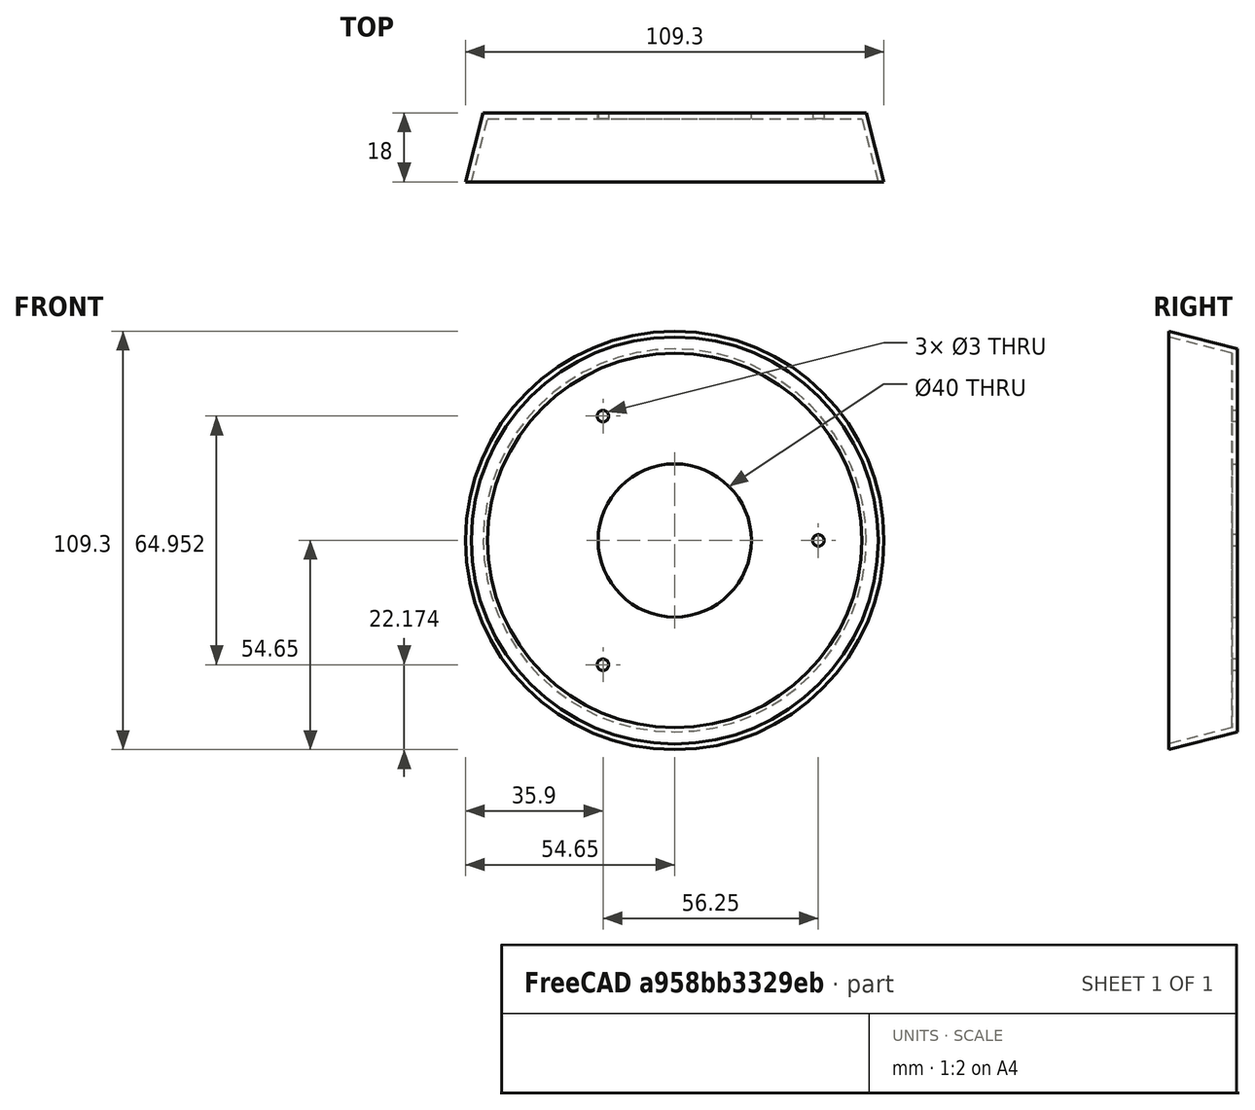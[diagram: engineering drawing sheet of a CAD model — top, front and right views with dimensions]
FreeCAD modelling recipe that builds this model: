
FCSTD DOCUMENT  (FreeCAD 0.18.4R)
Label: radiation_shield_dish
License: All rights reserved
LicenseURL: http://en.wikipedia.org/wiki/All_rights_reserved
objects: TechDraw::DrawViewDimension×5, Sketcher::SketchObject×4, TechDraw::DrawViewPart×3, PartDesign::Revolution×1, PartDesign::Hole×1, PartDesign::Pocket×1, PartDesign::Body×1, App::Part×1, TechDraw::DrawSVGTemplate×1, TechDraw::DrawViewAnnotation×1, TechDraw::DrawPage×1
note: 11 computed .brp shape members not serialized (recipe doc carries the construction recipe); baked Part::Feature solids carry a one-line shape summary decoded from their .brp

FEATURE [Sketcher::SketchObject] Sketch
  sketch-geometry (6):
    g0: LineSegment StartX=-54.6463 StartY=0 StartZ=0 EndX=-53.1463 EndY=0 EndZ=0
    g1: LineSegment StartX=-53.1463 StartY=0 StartZ=0 EndX=-48.8872 EndY=16.5 EndZ=0
    g2: LineSegment StartX=-48.8872 StartY=16.5 StartZ=0 EndX=0 EndY=16.5 EndZ=0
    g3: LineSegment StartX=0 StartY=16.5 StartZ=0 EndX=0 EndY=18 EndZ=0
    g4: LineSegment StartX=0 StartY=18 StartZ=0 EndX=-50 EndY=18 EndZ=0
    g5: LineSegment StartX=-50 StartY=18 StartZ=0 EndX=-54.6463 EndY=0 EndZ=0
  constraints (18):
    c: Coincident(g0,g1)
    c: Coincident(g2,g3)
    c: Coincident(g3,g4)
    c: Coincident(g4,g5)
    c: PointOnObject(g2,g-2)
    c: PointOnObject(g3,g-2)
    c: PointOnObject(g0,g-1)
    c: Coincident(g5,g0)
    c: PointOnObject(g0,g-1)
    c: Equal(g0,g3)
    c: DistanceX(g0,g0) = 1.5
    c: Parallel(g4,g-1)
    c: Parallel(g2,g-1)
    c: Coincident(g1,g2)
    c: DistanceX(g4,g4) = 50
    c: Parallel(g5,g1)
    c: DistanceY(g-1,g4) = 18
    c: Distance(g0,g4) = 18.59
FEATURE [PartDesign::Revolution] Revolution
  Angle = 360
  Axis = (0,1,0)
  Base = (0,0,0)
  Profile = -> Sketch
  ReferenceAxis = -> Sketch [V_Axis]
FEATURE [Sketcher::SketchObject] Sketch001
  MapMode = 5
  Placement = pos=(0,18,0) rot=(0,0.707107,0.707107;3.14159rad)
  Support = -> [Revolution]
  sketch-geometry (8):
    g0: LineSegment [constr] StartX=18.75 StartY=32.476 StartZ=0 EndX=-37.5 EndY=0 EndZ=0
    g1: LineSegment [constr] StartX=-37.5 StartY=0 StartZ=0 EndX=18.75 EndY=-32.476 EndZ=0
    g2: LineSegment [constr] StartX=18.75 StartY=-32.476 StartZ=0 EndX=18.75 EndY=32.476 EndZ=0
    g3: Circle [constr] CenterX=0 CenterY=0 CenterZ=0 NormalX=0 NormalY=0 NormalZ=1 AngleXU=0 Radius=37.5
    g4: Circle CenterX=-37.5 CenterY=0 CenterZ=0 NormalX=0 NormalY=0 NormalZ=1 AngleXU=0 Radius=3
    g5: Circle CenterX=18.75 CenterY=32.476 CenterZ=0 NormalX=0 NormalY=0 NormalZ=1 AngleXU=0 Radius=3
    g6: Circle CenterX=18.75 CenterY=-32.476 CenterZ=0 NormalX=0 NormalY=0 NormalZ=1 AngleXU=0 Radius=3
    g7: Circle CenterX=0 CenterY=0 CenterZ=0 NormalX=0 NormalY=0 NormalZ=1 AngleXU=0 Radius=20
  constraints (19):
    c: Coincident(g0,g1)
    c: Coincident(g1,g2)
    c: Coincident(g2,g0)
    c: Equal(g0,g1)
    c: Equal(g0,g2)
    c: PointOnObject(g0,g3)
    c: PointOnObject(g1,g3)
    c: PointOnObject(g2,g3)
    c: PointOnObject(g0,g-1)
    c: Coincident(g3,g-1)
    c: Radius(g3) = 37.5
    c: Radius(g5) = 3
    c: Coincident(g5,g0)
    c: Radius(g6) = 3
    c: Coincident(g6,g1)
    c: Radius(g4) = 3
    c: Coincident(g4,g0)
    c: Radius(g7) = 20  'Innenloch'
    c: Coincident(g7,g-1)
FEATURE [PartDesign::Hole] Hole
  BaseFeature = -> Revolution
  Depth = 25
  DepthType = 0
  Diameter = 3
  DrillPoint = 1
  DrillPointAngle = 118
  HoleCutCountersinkAngle = 90
  HoleCutDepth = 0
  HoleCutDiameter = 0
  HoleCutType = 0
  ModelActualThread = false
  Profile = -> Sketch001
  Tapered = false
  TaperedAngle = 90
  ThreadAngle = 0
  ThreadClass = 0
  ThreadCutOffInner = 0
  ThreadCutOffOuter = 0
  ThreadDirection = 0
  ThreadFit = 0
  ThreadPitch = 0
  ThreadSize = 0
  ThreadType = 0
  Threaded = false
FEATURE [Sketcher::SketchObject] Sketch002
  MapMode = 5
  Placement = pos=(0,18,0) rot=(0,0.707107,0.707107;3.14159rad)
  Support = -> [Hole]
  sketch-geometry (1):
    g0: Circle CenterX=0 CenterY=0 CenterZ=0 NormalX=0 NormalY=0 NormalZ=1 AngleXU=0 Radius=20
  constraints (2):
    c: Radius(g0) = 20  'Innenloch'
    c: Coincident(g0,g-1)
FEATURE [Sketcher::SketchObject] CopySketch002
  Placement = pos=(0,18,0) rot=(0,0.707107,0.707107;3.14159rad)
  sketch-geometry (1):
    g0: Circle CenterX=0 CenterY=0 CenterZ=0 NormalX=0 NormalY=0 NormalZ=1 AngleXU=0 Radius=20
  constraints (2):
    c: Radius(g0) = 20  'Innenloch'
    c: Coincident(g0,g-1)
FEATURE [PartDesign::Pocket] Pocket
  BaseFeature = -> Hole
  Length = 5
  Length2 = 100
  Profile = -> CopySketch002
  Type = 0
FEATURE [PartDesign::Body] Body
  Group = -> [Sketch,Revolution,Sketch001,Hole,Pocket]
  Origin = -> Origin001
  Tip = -> Pocket
FEATURE [App::Part] Part
  Group = -> [Body,CopySketch002]
  Origin = -> Origin
FEATURE [TechDraw::DrawSVGTemplate] Template
  EditableTexts = AUTHOR_NAME=Norman Rembarz; DN=DN; DRAWING_TITLE=RADIATION SHIELD - drill template; FC-DATE=31/10/2020; FC-REV=REV A; FC-SC=1:1; FC-SH=1; FC-SI=A4; FreeCAD_DRAWING=radiation shield for weather module; PN=RS-DU-1; SI-2=dish unit for stacking; SI-4=REGREEN PROJECT of EU
  Height = 297
  Orientation = 0
  Width = 210
FEATURE [TechDraw::DrawViewPart] View
  CoarseView = false
  Direction = (-0.382,0.884,-0.272)
  Focus = 100
  HardHidden = false
  IsoCount = 0
  IsoHidden = false
  IsoVisible = false
  LockPosition = false
  Perspective = false
  Rotation = 0
  Scale = 0.33
  ScaleType = 0
  SeamHidden = false
  SeamVisible = false
  SmoothHidden = false
  SmoothVisible = false
  Source = -> [Part]
  X = 39.7202
  Y = 99.1976
FEATURE [TechDraw::DrawViewPart] View001  label="Draufsicht"
  CoarseView = false
  Direction = (0,1,0)
  Focus = 100
  HardHidden = false
  IsoCount = 0
  IsoHidden = false
  IsoVisible = false
  LockPosition = false
  Perspective = false
  Rotation = 0
  ScaleType = 0
  SeamHidden = false
  SeamVisible = false
  SmoothHidden = false
  SmoothVisible = false
  Source = -> [Part]
  X = 108.714
  Y = 228.083
FEATURE [TechDraw::DrawViewDimension] Dimension
  Arbitrary = false
  FormatSpec = ⌀%.2f
  LockPosition = false
  MeasureType = 1
  OverTolerance = 0
  References2D = -> [View001]
  Rotation = 0
  ScaleType = 0
  Type = 5
  UnderTolerance = 0
  X = -66.3438
  Y = -36.0938
FEATURE [TechDraw::DrawViewDimension] Dimension001
  Arbitrary = false
  FormatSpec = ⌀%.2f
  LockPosition = false
  MeasureType = 1
  OverTolerance = 0
  References2D = -> [View001]
  Rotation = 0
  ScaleType = 0
  Type = 5
  UnderTolerance = 0
  X = 71.2586
  Y = 38.3533
FEATURE [TechDraw::DrawViewPart] View002
  CoarseView = false
  Direction = (0,0,-0.27)
  Focus = 100
  HardHidden = false
  IsoCount = 0
  IsoHidden = false
  IsoVisible = false
  LockPosition = false
  Perspective = false
  Rotation = 0
  ScaleType = 0
  SeamHidden = false
  SeamVisible = false
  SmoothHidden = false
  SmoothVisible = false
  Source = -> [Part]
  X = 109.445
  Y = 153.207
FEATURE [TechDraw::DrawViewDimension] Dimension002
  Arbitrary = false
  FormatSpec = %.2f
  LockPosition = false
  MeasureType = 1
  OverTolerance = 0
  References2D = -> [View002]
  Rotation = 0
  ScaleType = 0
  Type = 1
  UnderTolerance = 0
  X = 0.627599
  Y = -20.2968
FEATURE [TechDraw::DrawViewDimension] Dimension003
  Arbitrary = false
  FormatSpec = ⌀%.2f
  LockPosition = false
  MeasureType = 1
  OverTolerance = 0
  References2D = -> [View001]
  Rotation = 0
  ScaleType = 0
  Type = 5
  UnderTolerance = 0
  X = 55.8992
  Y = 49.3345
FEATURE [TechDraw::DrawViewDimension] Dimension004
  Arbitrary = false
  FormatSpec = %.2f
  LockPosition = false
  MeasureType = 1
  OverTolerance = 0
  References2D = -> [View001]
  Rotation = 0
  ScaleType = 0
  Type = 0
  UnderTolerance = 0
  X = 5.59534
  Y = -17.4316
FEATURE [TechDraw::DrawViewAnnotation] Annotation
  Font = osifont
  LineSpace = 80
  LockPosition = false
  MaxWidth = -1
  Rotation = 0
  ScaleType = 0
  Text = Caution: for some materials it is not recommended to use a drill - better use a milling tool
  TextSize = 2
  TextStyle = 0
  X = 133.242
  Y = 99.2335
FEATURE [TechDraw::DrawPage] Page  label="Zeichnung_dish"
  KeepUpdated = true
  ProjectionType = 0
  Template = -> Template
  Views = -> [View,View001,Dimension,Dimension001,View002,Dimension002,Dimension003,Dimension004,Annotation]
